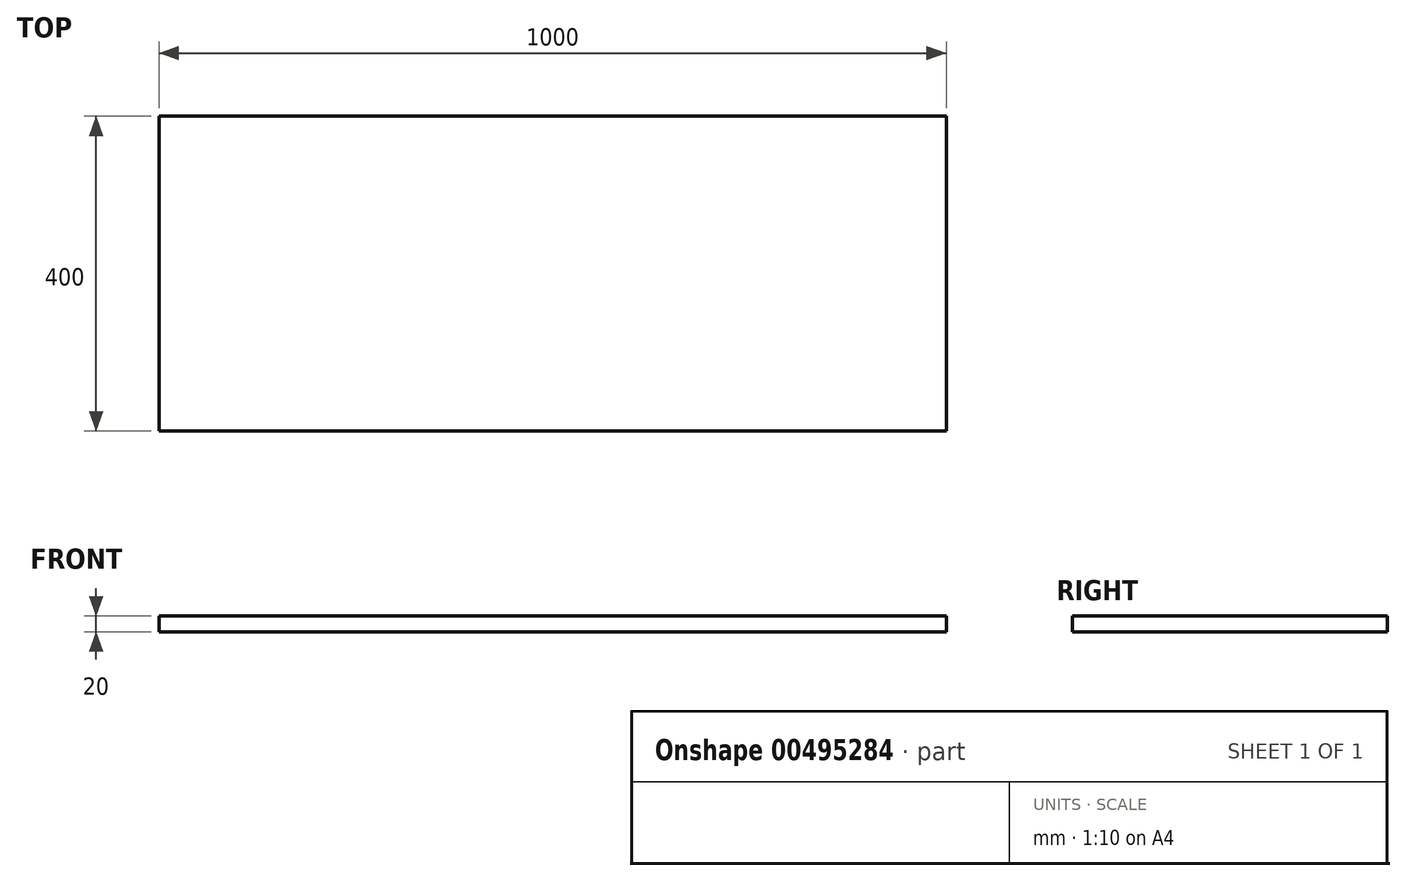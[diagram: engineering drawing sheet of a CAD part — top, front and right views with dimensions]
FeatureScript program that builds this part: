
annotation { "Feature Type Name" : "Feature", "Feature Type Description" : "" }
export const myFeature = defineFeature(function(context is Context, id is Id, definition is map)
    precondition{}
    {
        {
            var Q0;
            Q0=qCreatedBy(makeId("Top.planeOp"),FACE);
            var sketch = newSketch(context, id + "F0", { "sketchPlane" : qUnion([Q0])});
            skLineSegment(sketch, "E0.bottom", {"start": v(500, -200) * mm, "end": v(-500, -200) * mm});
            skLineSegment(sketch, "E0.top", {"start": v(500, 200) * mm, "end": v(-500, 200) * mm});
            skLineSegment(sketch, "E0.left", {"start": v(500, -200) * mm, "end": v(500, 200) * mm});
            skLineSegment(sketch, "E0.right", {"start": v(-500, -200) * mm, "end": v(-500, 200) * mm});
            skPoint(sketch, "E0.middle", {"position": v(0, 0) * mm});
            skSolve(sketch);
        }
        {
            var Q0;
            Q0 = qSketchRegion(id + "F0", true);
            extrude(context, id + "F1", {"entities" : qUnion([Q0]), "depth" : 20 * mm});
        }
    });
